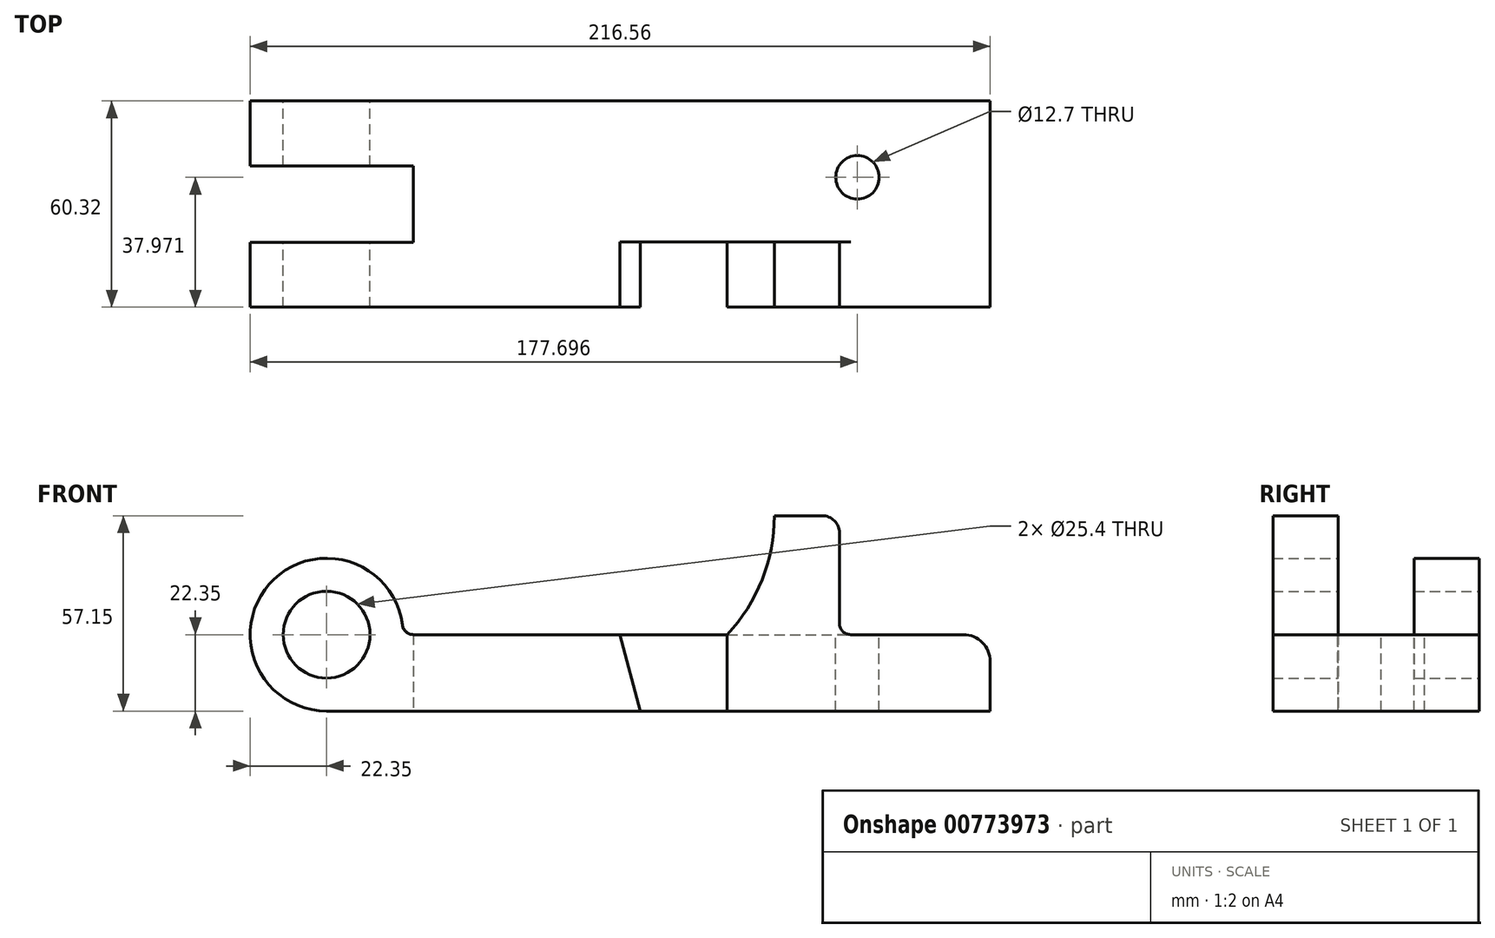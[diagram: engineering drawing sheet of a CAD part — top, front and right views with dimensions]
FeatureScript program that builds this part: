
annotation { "Feature Type Name" : "Feature", "Feature Type Description" : "" }
export const myFeature = defineFeature(function(context is Context, id is Id, definition is map)
    precondition{}
    {
        {
            var Q0;
            Q0=qCreatedBy(makeId("Front.planeOp"),FACE);
            var sketch = newSketch(context, id + "F0", { "sketchPlane" : qUnion([Q0])});
            skCircle(sketch, "E0", {"center": v(0, 0) * mm, "radius": 12.7 * mm});
            skCircle(sketch, "E1", {"center": v(0, 0) * mm, "radius": 22.35 * mm});
            skLineSegment(sketch, "E2", {"start": v(0, 0) * mm, "end": v(117.25, 0) * mm});
            skLineSegment(sketch, "E3", {"start": v(117.25, 0) * mm, "end": v(117.25, -22.35) * mm});
            skLineSegment(sketch, "E4", {"start": v(0, -22.35) * mm, "end": v(117.25, -22.35) * mm});
            skLineSegment(sketch, "E5", {"start": v(117.25, -22.35) * mm, "end": v(91.85, -22.35) * mm, "construction": true});
            skLineSegment(sketch, "E6", {"start": v(0, 0) * mm, "end": v(85.85, 0) * mm, "construction": true});
            skLineSegment(sketch, "E7", {"start": v(85.85, 0) * mm, "end": v(91.85, -22.35) * mm});
            skLineSegment(sketch, "E8", {"start": v(117.25, -22.35) * mm, "end": v(194.2, -22.35) * mm});
            skLineSegment(sketch, "E9", {"start": v(194.2, -22.35) * mm, "end": v(194.2, 0) * mm});
            skLineSegment(sketch, "E10", {"start": v(194.2, 0) * mm, "end": v(150.09, 0) * mm});
            skLineSegment(sketch, "E11", {"start": v(150.09, 0) * mm, "end": v(150.09, 34.8) * mm});
            skLineSegment(sketch, "E12", {"start": v(150.09, 34.8) * mm, "end": v(131.04, 34.8) * mm});
            skArc(sketch, "E13", {"start": v(117.25, 0) * mm, "mid": v(127.46, 16.08) * mm, "end": v(131.04, 34.8) * mm});
            skPoint(sketch, "E13.third.point", {"position": v(38.83, 64.22) * mm});
            skSolve(sketch);
        }
        {
            var Q0;
            Q0=makeQuery(id+"F0.imprint","IMPRINT",FACE,{"disambiguationData":[TD([[makeQuery(id+"F0.imprint","IMPRINT",EDGE,{"derivedFrom":sQuery(id+"F0.wireOp",EDGE,"E3")}),1.0]])]});
            extrude(context, id + "F1", {"entities" : qUnion([Q0]), "oppositeDirection" : true, "depth" : 30.16 * mm, "offsetDistance" : 25.4 * mm, "hasSecondDirection" : true, "secondDirectionOppositeDirection" : false, "secondDirectionDepth" : 30.16 * mm});
        }
        {
            var Q0;
            {var subQ0=sQuery(id+"F0.wireOp",EDGE,"E3");Q0=makeQuery(id+"F0.imprint","IMPRINT",FACE,{"disambiguationData":[TD([[makeQuery(id+"F0.imprint","IMPRINT",EDGE,{"derivedFrom":subQ0}),-1.0]])]});}
            extrude(context, id + "F2", {"entities" : qUnion([Q0]), "operationType" : NewBodyOperationType.ADD, "depth" : 11.1 * mm, "offsetDistance" : 25.4 * mm, "hasSecondDirection" : true, "secondDirectionOppositeDirection" : true, "secondDirectionDepth" : 30.16 * mm});
        }
        {
            var Q0;
            {var subQ5=sQuery(id+"F0.wireOp",EDGE,"E7");Q0=makeQuery(id+"F0.imprint","IMPRINT",FACE,{"disambiguationData":[TD([[makeQuery(id+"F0.imprint","IMPRINT",EDGE,{"derivedFrom":subQ5}),-1.0]])]});}
            var Q1;
            Q1=makeQuery(id+"F0.imprint","IMPRINT",FACE,{"disambiguationData":[TD([[makeQuery(id+"F0.imprint","IMPRINT",EDGE,{"derivedFrom":sQuery(id+"F0.wireOp",EDGE,"E0")}),-1.0]])]});
            extrude(context, id + "F3", {"entities" : qUnion([Q0, Q1]), "operationType" : NewBodyOperationType.ADD, "depth" : 30.16 * mm, "offsetDistance" : 25.4 * mm, "hasSecondDirection" : true, "secondDirectionOppositeDirection" : true, "secondDirectionDepth" : 30.16 * mm});
        }
        {
            var Q0;
            Q0=makeQuery(id+"F1.opExtrude","SWEPT_FACE",FACE,{"disambiguationData":[OSD([sQuery(id+"F0.wireOp",EDGE,"E11")])]});
            var sketch = newSketch(context, id + "F4", { "sketchPlane" : qUnion([Q0])});
            skLineSegment(sketch, "E14", {"start": v(-11.11, 34.8) * mm, "end": v(-11.11, 0) * mm});
            skSolve(sketch);
        }
        {
            var Q0;
            {var subQ0=sQuery(id+"F4.wireOp",EDGE,"E14");Q0=makeQuery(id+"F4.imprint","IMPRINT",FACE,{"disambiguationData":[TD([[makeQuery(id+"F4.imprint","IMPRINT",EDGE,{"derivedFrom":subQ0}),1.0]])]});}
            extrude(context, id + "F5", {"entities" : qUnion([Q0]), "operationType" : NewBodyOperationType.REMOVE, "oppositeDirection" : true, "depth" : 38.1 * mm, "offsetDistance" : 25.4 * mm});
        }
        {
            var Q0;
            Q0=qCreatedBy(makeId("Right.planeOp"),FACE);
            var sketch = newSketch(context, id + "F6", { "sketchPlane" : qUnion([Q0])});
            skLineSegment(sketch, "E15.bottom", {"start": v(0, 0) * mm, "end": v(11.16, 0) * mm});
            skLineSegment(sketch, "E15.top", {"start": v(0, 50.8) * mm, "end": v(11.16, 50.8) * mm});
            skLineSegment(sketch, "E15.left", {"start": v(0, 0) * mm, "end": v(0, 50.8) * mm});
            skLineSegment(sketch, "E15.right", {"start": v(11.16, 0) * mm, "end": v(11.16, 50.8) * mm});
            skLineSegment(sketch, "E16.bottom", {"start": v(0, 50.8) * mm, "end": v(-11.16, 50.8) * mm});
            skLineSegment(sketch, "E16.top", {"start": v(0, 0) * mm, "end": v(-11.16, 0) * mm});
            skLineSegment(sketch, "E16.left", {"start": v(0, 50.8) * mm, "end": v(0, 0) * mm});
            skLineSegment(sketch, "E16.right", {"start": v(-11.16, 50.8) * mm, "end": v(-11.16, 0) * mm});
            skLineSegment(sketch, "E17.bottom", {"start": v(-11.16, 0) * mm, "end": v(11.16, 0) * mm});
            skLineSegment(sketch, "E17.top", {"start": v(-11.16, -23.61) * mm, "end": v(11.16, -23.61) * mm});
            skLineSegment(sketch, "E17.left", {"start": v(-11.16, 0) * mm, "end": v(-11.16, -23.61) * mm});
            skLineSegment(sketch, "E17.right", {"start": v(11.16, 0) * mm, "end": v(11.16, -23.61) * mm});
            skSolve(sketch);
        }
        {
            var Q0;
            Q0=makeQuery(id+"F6.imprint","IMPRINT",FACE,{"disambiguationData":[TD([[makeQuery(id+"F6.imprint","IMPRINT",EDGE,{"derivedFrom":sQuery(id+"F6.wireOp",EDGE,"E15.bottom")}),1.0]])]});
            var Q1;
            Q1=makeQuery(id+"F6.imprint","IMPRINT",FACE,{"disambiguationData":[TD([[makeQuery(id+"F6.imprint","IMPRINT",EDGE,{"derivedFrom":sQuery(id+"F6.wireOp",EDGE,"E15.left")}),1.0]])]});
            var Q2;
            Q2=makeQuery(id+"F6.imprint","IMPRINT",FACE,{"disambiguationData":[TD([[makeQuery(id+"F6.imprint","IMPRINT",EDGE,{"derivedFrom":sQuery(id+"F6.wireOp",EDGE,"E15.bottom")}),-1.0]])]});
            extrude(context, id + "F7", {"entities" : qUnion([Q0, Q1, Q2]), "operationType" : NewBodyOperationType.REMOVE, "oppositeDirection" : true, "depth" : 25.4 * mm, "offsetDistance" : 25.4 * mm, "hasSecondDirection" : true, "secondDirectionOppositeDirection" : false, "secondDirectionDepth" : 25.4 * mm});
        }
        {
            var Q0;
            {var subQ0=sQuery(id+"F0.wireOp",EDGE,"E10");var subQ1=sQuery(id+"F0.wireOp",EDGE,"E2");Q0=makeQuery(id+"F5.boolean.opBoolean","MERGE",FACE,{"derivedFrom":[makeQuery(id+"F1.opExtrude","SWEPT_FACE",FACE,{"disambiguationData":[OSD([subQ0])]}),makeQuery(id+"F3.boolean.opBoolean","MERGE",FACE,{"derivedFrom":[makeQuery(id+"F2.opExtrude","SWEPT_FACE",FACE,{"disambiguationData":[OSD([subQ1])]}),makeQuery(id+"F3.opExtrude","SWEPT_FACE",FACE,{"disambiguationData":[OSD([subQ1])]})]}),makeQuery(id+"F5.opExtrude","SWEPT_FACE",FACE,{"disambiguationData":[OSD([subQ0,sQuery(id+"F0.wireOp",EDGE,"E11")])]})]});}
            var sketch = newSketch(context, id + "F8", { "sketchPlane" : qUnion([Q0])});
            skLineSegment(sketch, "E18", {"start": v(194.2, 30.16) * mm, "end": v(155.35, 30.16) * mm, "construction": true});
            skLineSegment(sketch, "E19", {"start": v(155.35, 30.16) * mm, "end": v(155.35, 7.81) * mm, "construction": true});
            skCircle(sketch, "E20", {"center": v(155.35, 7.81) * mm, "radius": 6.35 * mm});
            skSolve(sketch);
        }
        {
            var Q0;
            Q0=makeQuery(id+"F8.imprint","IMPRINT",FACE,{"disambiguationData":[TD([[makeQuery(id+"F8.imprint","IMPRINT",EDGE,{"derivedFrom":sQuery(id+"F8.wireOp",EDGE,"E20")}),1.0]])]});
            extrude(context, id + "F9", {"entities" : qUnion([Q0]), "operationType" : NewBodyOperationType.REMOVE, "oppositeDirection" : true, "depth" : 25.4 * mm, "offsetDistance" : 25.4 * mm});
        }
        {
            var Q0;
            Q0=makeQuery(id+"F1.opExtrude","SWEPT_EDGE",EDGE,{"disambiguationData":[OSD([sQuery(id+"F0.wireOp",EDGE,"E9"),sQuery(id+"F0.wireOp",EDGE,"E10")])]});
            fillet(context, id + "F10", {"entities" : qUnion([Q0]), "radius" : 7.87 * mm, "tangentPropagation" : true, "allowEdgeOverflow" : false});
        }
        {
            var Q0;
            Q0=makeQuery(id+"F1.opExtrude","SWEPT_EDGE",EDGE,{"disambiguationData":[OSD([sQuery(id+"F0.wireOp",EDGE,"E11"),sQuery(id+"F0.wireOp",EDGE,"E12")])]});
            fillet(context, id + "F11", {"entities" : qUnion([Q0]), "radius" : 5.08 * mm, "tangentPropagation" : true, "allowEdgeOverflow" : false});
        }
        {
            var Q0;
            {var subQ0=sQuery(id+"F0.wireOp",EDGE,"E1");var subQ1=sQuery(id+"F0.wireOp",EDGE,"E2");Q0=makeQuery(id+"F7.boolean.opBoolean","SPLIT",EDGE,{"disambiguationData":[TD([makeQuery(id+"F7.opExtrude","SWEPT_FACE",FACE,{"disambiguationData":[OSD([sQuery(id+"F6.wireOp",EDGE,"E16.right"),sQuery(id+"F6.wireOp",EDGE,"E17.left")])]})])],"derivedFrom":makeQuery(id+"F3.opExtrude","SWEPT_EDGE",EDGE,{"disambiguationData":[OSD([subQ0,subQ1])]})});}
            var Q1;
            Q1=makeQuery(id+"F1.opExtrude","SWEPT_EDGE",EDGE,{"disambiguationData":[OSD([sQuery(id+"F0.wireOp",EDGE,"E10"),sQuery(id+"F0.wireOp",EDGE,"E11")])]});
            fillet(context, id + "F12", {"entities" : qUnion([Q0, Q1]), "radius" : 3.3 * mm, "tangentPropagation" : true, "allowEdgeOverflow" : false});
        }
    });
